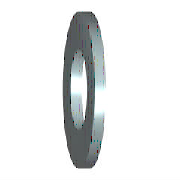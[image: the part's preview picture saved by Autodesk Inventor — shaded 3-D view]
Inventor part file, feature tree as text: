
AUTODESK INVENTOR PART (.ipt)
format: ipt  version: 2024.3 (Build 283343000, 343)  size: 105,472 bytes
history: native  units: mm (DEFAULTED — no unit token found)
features: other x1, plane x1
ambient origin geometry x7: Origin, YZ Plane, XY Plane, X Axis, Y Axis, Z Axis, Center Point
bodies: Solid1 (feature_tree), Body (feature_tree)
feature tree (2):
  other  "Work Axis1"
  plane  "Work Plane1"
